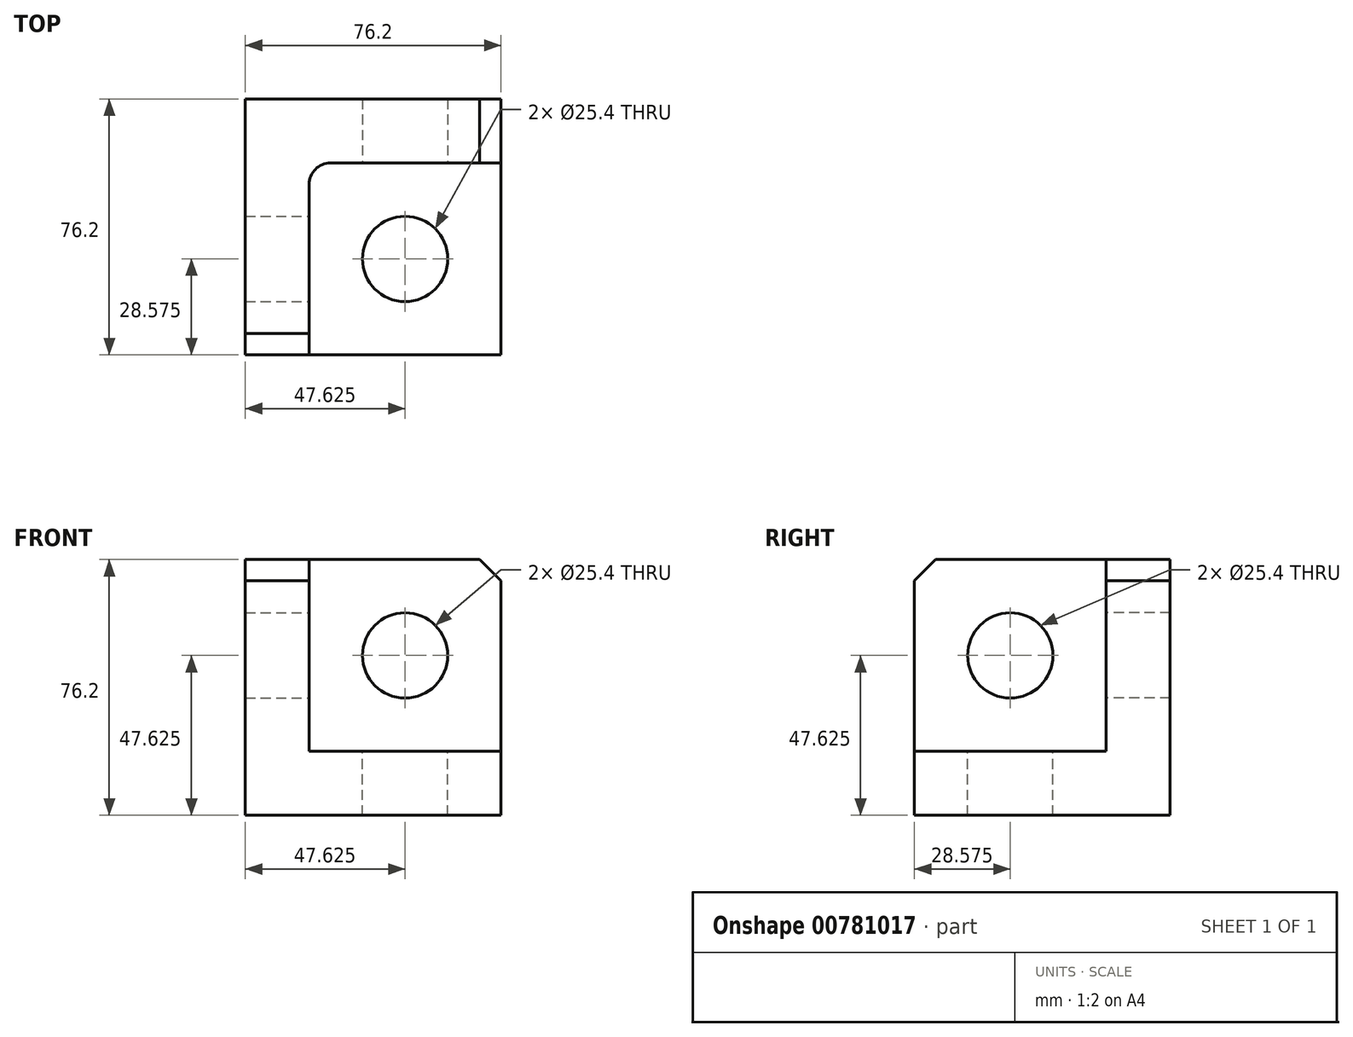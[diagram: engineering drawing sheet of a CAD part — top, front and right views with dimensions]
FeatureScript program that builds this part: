
annotation { "Feature Type Name" : "Feature", "Feature Type Description" : "" }
export const myFeature = defineFeature(function(context is Context, id is Id, definition is map)
    precondition{}
    {
        {
            var Q0;
            Q0=qCreatedBy(makeId("Front.planeOp"),FACE);
            var sketch = newSketch(context, id + "F0", { "sketchPlane" : qUnion([Q0])});
            skLineSegment(sketch, "E0.bottom", {"start": v(0, 0) * mm, "end": v(76.2, 0) * mm});
            skLineSegment(sketch, "E0.top", {"start": v(0, 76.2) * mm, "end": v(76.2, 76.2) * mm});
            skLineSegment(sketch, "E0.left", {"start": v(0, 0) * mm, "end": v(0, 76.2) * mm});
            skLineSegment(sketch, "E0.right", {"start": v(76.2, 0) * mm, "end": v(76.2, 76.2) * mm});
            skSolve(sketch);
        }
        {
            var Q0;
            Q0 = qSketchRegion(id + "F0", true);
            extrude(context, id + "F1", {"entities" : qUnion([Q0]), "depth" : 76.2 * mm, "offsetDistance" : 25.4 * mm});
        }
        {
            var Q0;
            Q0=makeQuery(id+"F1.opExtrude","CAP_FACE",FACE,{"disambiguationData":[OSD([sQuery(id+"F0.wireOp",EDGE,"E0.bottom"),sQuery(id+"F0.wireOp",EDGE,"E0.top"),sQuery(id+"F0.wireOp",EDGE,"E0.left"),sQuery(id+"F0.wireOp",EDGE,"E0.right")])],"isStart":false});
            var sketch = newSketch(context, id + "F2", { "sketchPlane" : qUnion([Q0])});
            skLineSegment(sketch, "E1.bottom", {"start": v(76.2, 76.2) * mm, "end": v(19.05, 76.2) * mm});
            skLineSegment(sketch, "E1.top", {"start": v(76.2, 19.05) * mm, "end": v(19.05, 19.05) * mm});
            skLineSegment(sketch, "E1.left", {"start": v(76.2, 76.2) * mm, "end": v(76.2, 19.05) * mm});
            skLineSegment(sketch, "E1.right", {"start": v(19.05, 76.2) * mm, "end": v(19.05, 19.05) * mm});
            skSolve(sketch);
        }
        {
            var Q0;
            Q0 = qSketchRegion(id + "F2", true);
            extrude(context, id + "F3", {"entities" : qUnion([Q0]), "operationType" : NewBodyOperationType.REMOVE, "oppositeDirection" : true, "depth" : 57.15 * mm, "offsetDistance" : 25.4 * mm});
        }
        {
            var Q0;
            Q0=makeQuery(id+"F3.boolean.opBoolean","COPY",FACE,{"derivedFrom":makeQuery(id+"F3.opExtrude","SWEPT_FACE",FACE,{"disambiguationData":[OSD([sQuery(id+"F2.wireOp",EDGE,"E1.top")])]})});
            var sketch = newSketch(context, id + "F4", { "sketchPlane" : qUnion([Q0])});
            skCircle(sketch, "E2", {"center": v(47.63, -47.62) * mm, "radius": 12.7 * mm});
            skSolve(sketch);
        }
        {
            var Q0;
            Q0 = qSketchRegion(id + "F4", true);
            extrude(context, id + "F5", {"entities" : qUnion([Q0]), "operationType" : NewBodyOperationType.REMOVE, "oppositeDirection" : true, "depth" : 19.05 * mm, "offsetDistance" : 25.4 * mm});
        }
        {
            var Q0;
            Q0=makeQuery(id+"F3.boolean.opBoolean","COPY",FACE,{"derivedFrom":makeQuery(id+"F3.opExtrude","SWEPT_FACE",FACE,{"disambiguationData":[OSD([sQuery(id+"F2.wireOp",EDGE,"E1.right")])]})});
            var sketch = newSketch(context, id + "F6", { "sketchPlane" : qUnion([Q0])});
            skCircle(sketch, "E3", {"center": v(-47.62, 47.62) * mm, "radius": 12.7 * mm});
            skSolve(sketch);
        }
        {
            var Q0;
            Q0 = qSketchRegion(id + "F6", true);
            extrude(context, id + "F7", {"entities" : qUnion([Q0]), "operationType" : NewBodyOperationType.REMOVE, "oppositeDirection" : true, "depth" : 19.05 * mm, "offsetDistance" : 25.4 * mm});
        }
        {
            var Q0;
            Q0=makeQuery(id+"F3.boolean.opBoolean","COPY",FACE,{"derivedFrom":makeQuery(id+"F3.opExtrude","CAP_FACE",FACE,{"disambiguationData":[OSD([sQuery(id+"F2.wireOp",EDGE,"E1.bottom"),sQuery(id+"F2.wireOp",EDGE,"E1.top"),sQuery(id+"F2.wireOp",EDGE,"E1.left"),sQuery(id+"F2.wireOp",EDGE,"E1.right")])],"isStart":false})});
            var sketch = newSketch(context, id + "F8", { "sketchPlane" : qUnion([Q0])});
            skCircle(sketch, "E4", {"center": v(47.62, 47.62) * mm, "radius": 12.7 * mm});
            skSolve(sketch);
        }
        {
            var Q0;
            Q0 = qSketchRegion(id + "F8", true);
            extrude(context, id + "F9", {"entities" : qUnion([Q0]), "operationType" : NewBodyOperationType.REMOVE, "oppositeDirection" : true, "depth" : 19.05 * mm, "offsetDistance" : 25.4 * mm});
        }
        {
            var Q0;
            Q0=makeQuery(id+"F1.opExtrude","CAP_EDGE",EDGE,{"disambiguationData":[OSD([sQuery(id+"F0.wireOp",EDGE,"E0.top")])],"isStart":false});
            var Q1;
            Q1=makeQuery(id+"F1.opExtrude","SWEPT_EDGE",EDGE,{"disambiguationData":[OSD([sQuery(id+"F0.wireOp",EDGE,"E0.top"),sQuery(id+"F0.wireOp",EDGE,"E0.right")])]});
            chamfer(context, id + "F10", {"entities" : qUnion([Q0, Q1]), "width" : 6.35 * mm, "tangentPropagation" : true});
        }
        {
            var Q0;
            Q0=makeQuery(id+"F3.boolean.opBoolean","COPY",EDGE,{"derivedFrom":makeQuery(id+"F3.opExtrude","CAP_EDGE",EDGE,{"disambiguationData":[OSD([sQuery(id+"F2.wireOp",EDGE,"E1.right")])],"isStart":false})});
            fillet(context, id + "F11", {"entities" : qUnion([Q0]), "radius" : 6.35 * mm, "tangentPropagation" : true, "allowEdgeOverflow" : false});
        }
    });
